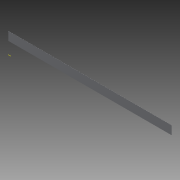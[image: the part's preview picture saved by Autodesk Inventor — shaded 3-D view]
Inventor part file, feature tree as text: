
AUTODESK INVENTOR PART (.ipt)
format: ipt  version: 2013 (Build 170138000, 138)  size: 101,888 bytes
history: native  units: in
note: dims shown in document units (in); Inventor stores cm internally (conversion verified against a paired STEP export)
features: extrude x4, sketch x4, plane x1
ambient origin geometry x8: Origin, YZ Plane, XZ Plane, XY Plane, X Axis, Y Axis, Z Axis, Center Point
bodies: Solid1 (feature_tree)
feature tree (9):
  plane  "Work Plane1"
  extrude  "Extrusion1"  Depth=1.0in
  extrude  "Extrusion2"  Depth=18.99in
  extrude  "Extrusion3"  Depth=0.01in TaperAngle=0.0deg
  extrude  "Extrusion4"  Depth=0.01in TaperAngle=0.0deg
  sketch  "Sketch1"  dims[d0=18.99in d1=1.0in]
  sketch  "Sketch2"  dims[d2=0.25in d3=18.99in]
  sketch  "Sketch3"  dims[d4=1.0in d5=0.01in d6=0.0in]
  sketch  "Sketch4"  dims[d7=0.01in d8=0.0in d9=0.01in d10=0.0in d11=0.01in d12=1.0in d13=0.01in d14=1.0in d15=1.0in d16=0.0in]
